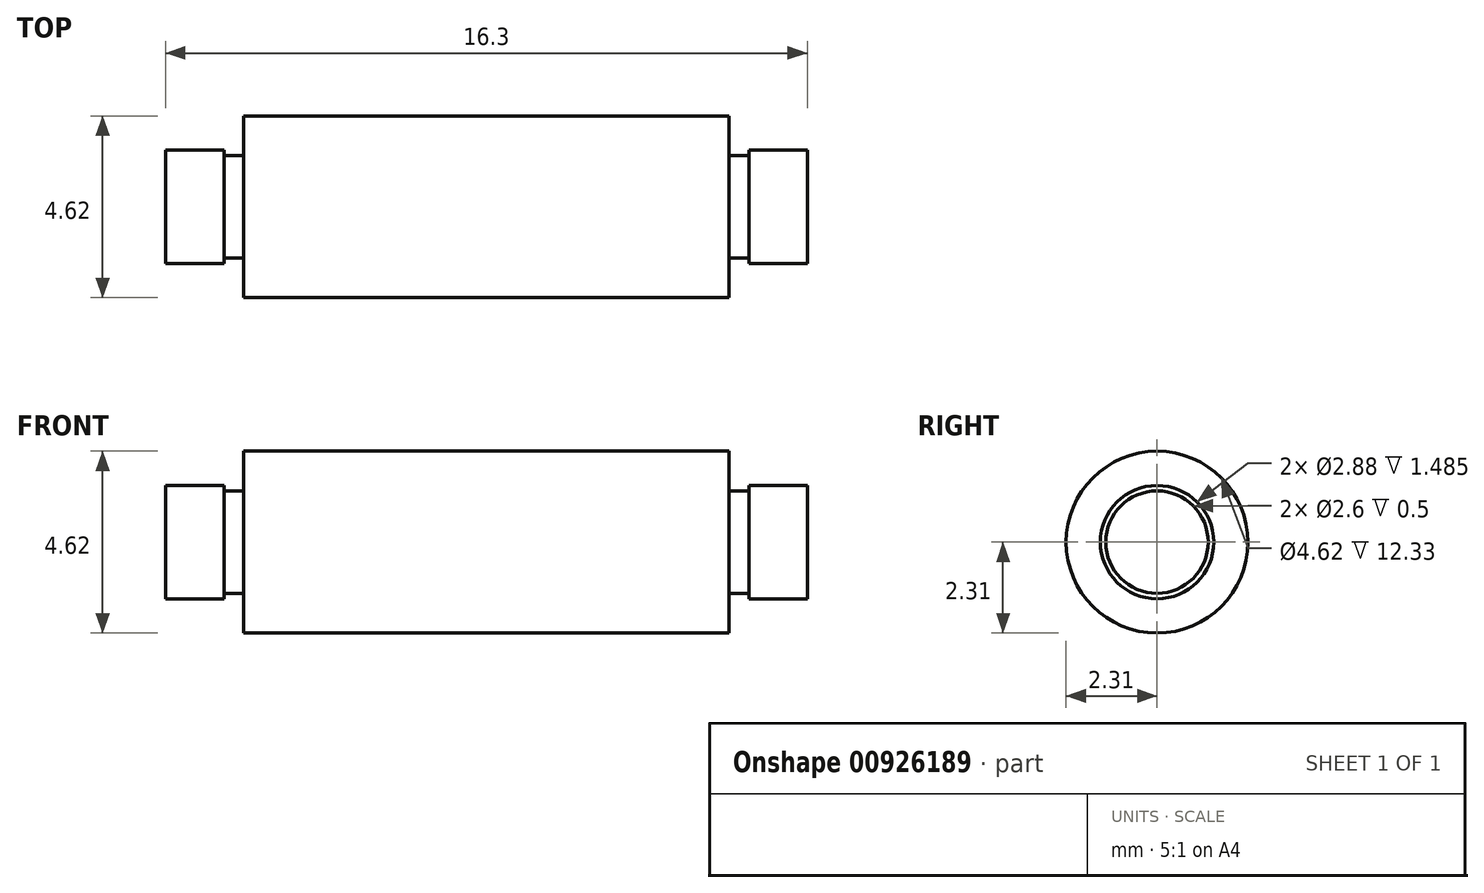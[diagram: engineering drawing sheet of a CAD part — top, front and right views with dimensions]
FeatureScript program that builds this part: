
annotation { "Feature Type Name" : "Feature", "Feature Type Description" : "" }
export const myFeature = defineFeature(function(context is Context, id is Id, definition is map)
    precondition{}
    {
        {
            var Q0;
            Q0=qCreatedBy(makeId("Front.planeOp"),FACE);
            var sketch = newSketch(context, id + "F0", { "sketchPlane" : qUnion([Q0])});
            skLineSegment(sketch, "E0", {"start": v(0, 2.31) * mm, "end": v(-6.17, 2.31) * mm});
            skLineSegment(sketch, "E1", {"start": v(-6.17, 2.3) * mm, "end": v(-6.17, 1.3) * mm});
            skLineSegment(sketch, "E2", {"start": v(-6.17, 1.3) * mm, "end": v(-6.67, 1.3) * mm});
            skLineSegment(sketch, "E3", {"start": v(-6.67, 1.3) * mm, "end": v(-6.67, 1.44) * mm});
            skLineSegment(sketch, "E4", {"start": v(-8.15, 0) * mm, "end": v(-8.15, 0.23) * mm});
            skLineSegment(sketch, "E5", {"start": v(0, 3.94) * mm, "end": v(0, -3.56) * mm, "construction": true});
            skLineSegment(sketch, "E6.MirrorCS", {"start": v(8.15, 0) * mm, "end": v(8.15, 0.23) * mm});
            skLineSegment(sketch, "E7.MirrorCS", {"start": v(6.67, 1.3) * mm, "end": v(6.67, 1.44) * mm});
            skLineSegment(sketch, "E8.MirrorCS", {"start": v(6.17, 1.3) * mm, "end": v(6.67, 1.3) * mm});
            skLineSegment(sketch, "E9.MirrorCS", {"start": v(6.17, 2.3) * mm, "end": v(6.17, 1.3) * mm});
            skLineSegment(sketch, "E10.MirrorCS", {"start": v(0, 2.31) * mm, "end": v(6.17, 2.31) * mm});
            skLineSegment(sketch, "E11", {"start": v(-10.73, 0) * mm, "end": v(10.4, 0) * mm, "construction": true});
            skLineSegment(sketch, "E12", {"start": v(-6.67, 1.44) * mm, "end": v(-8.15, 1.44) * mm});
            skLineSegment(sketch, "E13", {"start": v(-8.15, 1.44) * mm, "end": v(-8.15, 0.23) * mm});
            skLineSegment(sketch, "E14", {"start": v(6.67, 1.44) * mm, "end": v(8.15, 1.44) * mm});
            skLineSegment(sketch, "E15", {"start": v(8.15, 1.44) * mm, "end": v(8.15, 0.23) * mm});
            skSolve(sketch);
        }
        {
            var Q0;
            Q0=sQuery(id+"F0.wireOp",EDGE,"E0");
            var Q1;
            Q1=sQuery(id+"F0.wireOp",EDGE,"E1");
            var Q2;
            Q2=sQuery(id+"F0.wireOp",EDGE,"E2");
            var Q3;
            Q3=sQuery(id+"F0.wireOp",EDGE,"E10.MirrorCS");
            var Q4;
            Q4=sQuery(id+"F0.wireOp",EDGE,"E8.MirrorCS");
            var Q5;
            Q5=sQuery(id+"F0.wireOp",EDGE,"5832287f-8c61-4bc1-b951-138f5d6e948c0.MirrorCS");
            var Q6;
            Q6=sQuery(id+"F0.wireOp",EDGE,"2ut1R0WN-s9Rp-qwpJ-q27S-DyiSHYH6ZS53");
            var Q7;
            Q7=sQuery(id+"F0.wireOp",EDGE,"E3");
            var Q8;
            Q8=sQuery(id+"F0.wireOp",EDGE,"E4");
            var Q9;
            Q9=sQuery(id+"F0.wireOp",EDGE,"E7.MirrorCS");
            var Q10;
            Q10=sQuery(id+"F0.wireOp",EDGE,"E6.MirrorCS");
            var Q11;
            Q11=sQuery(id+"F0.wireOp",EDGE,"E9.MirrorCS");
            var Q12;
            Q12=sQuery(id+"F0.wireOp",EDGE,"E12");
            var Q13;
            Q13=sQuery(id+"F0.wireOp",EDGE,"E14");
            var Q14;
            Q14=sQuery(id+"F0.wireOp",EDGE,"E15");
            var Q15;
            Q15=sQuery(id+"F0.wireOp",EDGE,"E13");
            var Q16;
            Q16=sQuery(id+"F0.wireOp",EDGE,"E11");
            revolve(context, id + "F1", {"bodyType" : ToolBodyType.SURFACE, "surfaceOperationType" : NewSurfaceOperationType.NEW, "surfaceEntities" : qUnion([Q0, Q1, Q2, Q3, Q4, Q5, Q6, Q7, Q8, Q9, Q10, Q11, Q12, Q13, Q14, Q15]), "axis" : qUnion([Q16]), "revolveType" : RevolveType.FULL});
        }
    });
